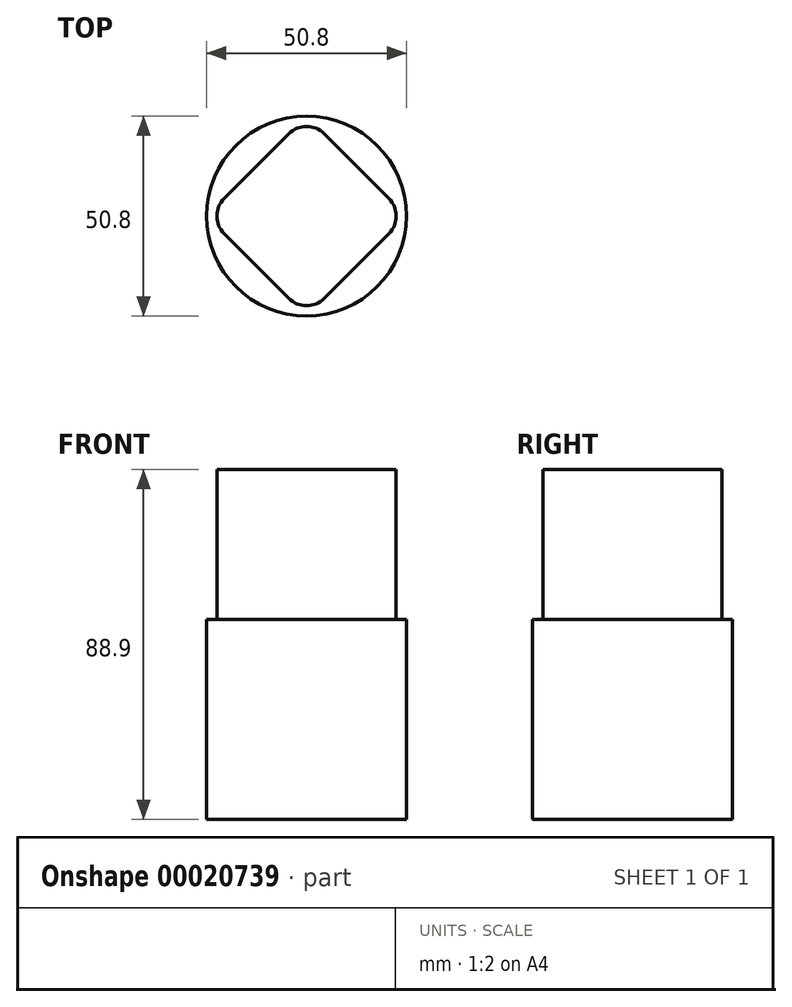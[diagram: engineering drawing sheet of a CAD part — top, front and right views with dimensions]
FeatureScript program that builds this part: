
annotation { "Feature Type Name" : "Feature", "Feature Type Description" : "" }
export const myFeature = defineFeature(function(context is Context, id is Id, definition is map)
    precondition{}
    {
        {
            var Q0;
            Q0=qCreatedBy(makeId("Top.planeOp"),FACE);
            var sketch = newSketch(context, id + "F0", { "sketchPlane" : qUnion([Q0])});
            skCircle(sketch, "E0", {"center": v(0, 10.66) * mm, "radius": 25.4 * mm});
            skSolve(sketch);
        }
        {
            var Q0;
            Q0=makeQuery(id+"F0.imprint","IMPRINT",FACE,{"disambiguationData":[TD([[makeQuery(id+"F0.imprint","IMPRINT",EDGE,{"derivedFrom":sQuery(id+"F0.wireOp",EDGE,"E0")}),1.0]])]});
            extrude(context, id + "F1", {"entities" : qUnion([Q0]), "depth" : 50.8 * mm});
        }
        {
            var Q0;
            Q0=makeQuery(id+"F1.opExtrude","CAP_FACE",FACE,{"disambiguationData":[OSD([sQuery(id+"F0.wireOp",EDGE,"E0")])],"isStart":false});
            var sketch = newSketch(context, id + "F2", { "sketchPlane" : qUnion([Q0])});
            skLineSegment(sketch, "E1", {"start": v(-20.9, 15.15) * mm, "end": v(-4.5, 31.57) * mm});
            skLineSegment(sketch, "E2", {"start": v(4.5, -10.25) * mm, "end": v(20.9, 6.17) * mm});
            skLineSegment(sketch, "E3", {"start": v(20.9, 15.15) * mm, "end": v(4.5, 31.57) * mm});
            skLineSegment(sketch, "E4", {"start": v(-20.9, 6.17) * mm, "end": v(-4.5, -10.25) * mm});
            skPoint(sketch, "E5.visualSharp", {"position": v(0, 36.06) * mm});
            skArc(sketch, "E5.filletArc", {"start": v(4.5, 31.57) * mm, "mid": v(0, 33.43) * mm, "end": v(-4.5, 31.57) * mm});
            skPoint(sketch, "E6.visualSharp", {"position": v(25.4, 10.66) * mm});
            skArc(sketch, "E6.filletArc", {"start": v(20.9, 6.17) * mm, "mid": v(22.77, 10.66) * mm, "end": v(20.9, 15.15) * mm});
            skPoint(sketch, "E7.visualSharp", {"position": v(0, -14.74) * mm});
            skArc(sketch, "E7.filletArc", {"start": v(-4.5, -10.25) * mm, "mid": v(0, -12.11) * mm, "end": v(4.5, -10.25) * mm});
            skPoint(sketch, "E8.visualSharp", {"position": v(-25.4, 10.66) * mm});
            skArc(sketch, "E8.filletArc", {"start": v(-20.9, 15.15) * mm, "mid": v(-22.77, 10.66) * mm, "end": v(-20.9, 6.17) * mm});
            skSolve(sketch);
        }
        {
            var Q0;
            Q0=makeQuery(id+"F2.imprint","IMPRINT",FACE,{"disambiguationData":[TD([[makeQuery(id+"F2.imprint","IMPRINT",EDGE,{"derivedFrom":sQuery(id+"F2.wireOp",EDGE,"E1")}),-1.0]])]});
            extrude(context, id + "F3", {"entities" : qUnion([Q0]), "operationType" : NewBodyOperationType.ADD, "depth" : 38.1 * mm});
        }
    });
